# Revit family: 16-649L
name_source: partatom
category: Specialty Equipment
revit_build: Autodesk Revit 2018 (Build: 20170223_1515(x64)
units: mm (PartAtom-declared; Revit-internal decimal feet)

## family parameters
Always vertical = Yes
Cut with Voids When Loaded = No
OmniClass Number = 23.45.05.14
OmniClass Title = Plumbing Fixtures - Sanitary Washing Units
Part Type = Normal
Room Calculation Point = No
Round Connector Dimension = Use Diameter
Shared = No
Work Plane-Based = No

## types (1)
- 16-649L
    Assembly Code = D2010400
    Cold Water Connection Height = 0' - 0"
    Cold Water Flow = 2 GPM
    Cold Water RI Height = 0' - 0"
    Cold Water Size = 1"
    Description = Single Hole Deck Mount
    Foodservice Equipment Identifier = Yes
    Hot Water Connection Height = 0' - 0"
    Hot Water Flow = 2 GPM
    Hot Water RI Height = 0' - 0"
    Hot Water Size = 1"
    Inlet Size = 0' - 0 1/2"
    Manufacturer = Krowne Metal
    Model = 16-649L

## geometry (parser evidence)
native form markers: Sweep x2
no freeform markers — native parametric forms only
